# Revit family: MS934214SF
name_source: partatom
category: Plumbing Fixtures
revit_build: Autodesk Revit 2014 (Build: 20130308_1515(x64)
units: mm (PartAtom-declared; Revit-internal decimal feet)

## types (1)
- MS934214SF
    Codes/Standards = • Meets and exceeds ASME A112.19.2/CSA B45.1, • Certifications: IAPMO(cUPC), State of Massachusetts , City of Los Angeles, and others • Code compliance: UPC, IPC, NSPC, NPC Canada, and others • ADA compliant (when installed with trip lever located on the approach side)
    Colors/Finishes = Standard #01 Cotton #03 Bone #11 Colonial White #12 Sedona Beige #51 Ebony
    Manufacturer = TOTO USA
    Model = MS934214SF
    Specifications = • Water Use 1.6 GPF/6.0LPF • Flush System G-Max® • Min. Water Pressure 8 psi (static) • Water Surface 10-3/4" x 8-1/4" • Trap Diameter 2-1/8" • Rough-in 12", 10" and 14" optional • Trap Seal 2-1/4"  • Warranty One Year Limited Warranty  • Material Vitreous china • Shipping Weight 120 lbs. • Shipping Dimensions 32" L X 20"W X 17-3/4" H1 X 28-3/4" H2
    trap seal = 0' - 2 1/8"

## geometry (parser evidence)
native form markers: Sweep x6
no freeform markers — native parametric forms only
